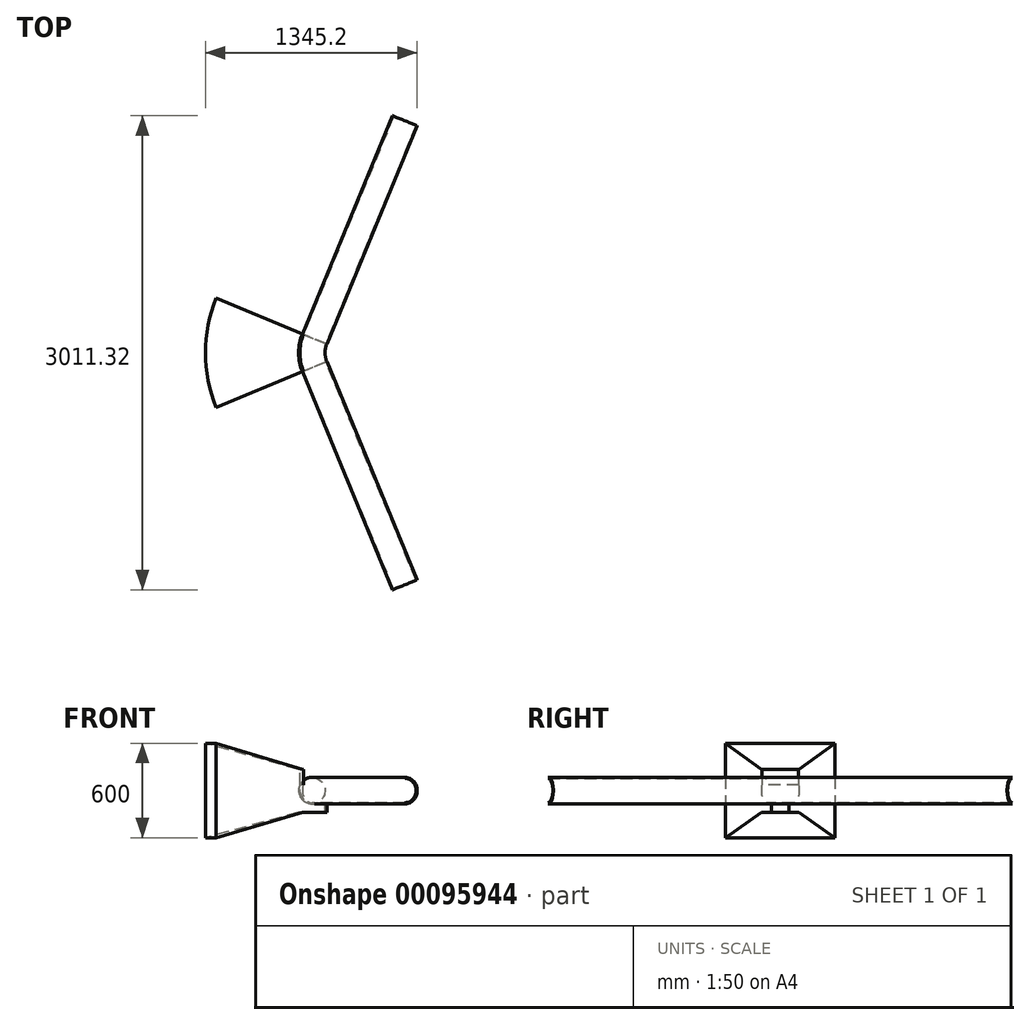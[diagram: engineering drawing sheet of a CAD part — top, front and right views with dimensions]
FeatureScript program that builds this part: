
annotation { "Feature Type Name" : "Feature", "Feature Type Description" : "" }
export const myFeature = defineFeature(function(context is Context, id is Id, definition is map)
    precondition{}
    {
        {
            var Q0;
            Q0=qCreatedBy(makeId("Front.planeOp"),FACE);
            var sketch = newSketch(context, id + "F0", { "sketchPlane" : qUnion([Q0])});
            skCircle(sketch, "E0", {"center": v(0, 0) * mm, "radius": 77.05 * mm});
            skCircle(sketch, "E1.0", {"center": v(0, 0) * mm, "radius": 84.15 * mm});
            skLineSegment(sketch, "E2", {"start": v(229, 111.57) * mm, "end": v(229, -112.44) * mm, "construction": true});
            skSolve(sketch);
        }
        {
            var Q0;
            Q0=makeQuery(id+"F0.imprint","IMPRINT",FACE,{"disambiguationData":[TD([[makeQuery(id+"F0.imprint","IMPRINT",EDGE,{"derivedFrom":sQuery(id+"F0.wireOp",EDGE,"E0")}),-1.0]])]});
            var Q1;
            Q1=sQuery(id+"F0.wireOp",EDGE,"E2");
            revolve(context, id + "F1", {"entities" : qUnion([Q0]), "axis" : qUnion([Q1]), "revolveType" : RevolveType.SYMMETRIC, "angle" : 45 * degree});
        }
        {
            var Q0;
            Q0=makeQuery(id+"F1.opRevolve","CAP_FACE",FACE,{"disambiguationData":[OSD([sQuery(id+"F0.wireOp",EDGE,"E0"),sQuery(id+"F0.wireOp",EDGE,"E1.0")])],"isStart":true});
            var sketch = newSketch(context, id + "F2", { "sketchPlane" : qUnion([Q0])});
            skCircle(sketch, "E3.0", {"center": v(-17.43, 0) * mm, "radius": 84.15 * mm});
            skCircle(sketch, "E4.0", {"center": v(-17.43, 0) * mm, "radius": 77.05 * mm});
            skSolve(sketch);
        }
        {
            var Q0;
            Q0=makeQuery(id+"F2.imprint","IMPRINT",FACE,{"disambiguationData":[TD([[makeQuery(id+"F2.imprint","IMPRINT",EDGE,{"derivedFrom":sQuery(id+"F2.wireOp",EDGE,"E3.0")}),1.0]])]});
            extrude(context, id + "F3", {"entities" : qUnion([Q0]), "operationType" : NewBodyOperationType.ADD, "depth" : 1500 * mm});
        }
        {
            var Q0;
            Q0=makeQuery(id+"F1.opRevolve","CAP_FACE",FACE,{"disambiguationData":[OSD([sQuery(id+"F0.wireOp",EDGE,"E0"),sQuery(id+"F0.wireOp",EDGE,"E1.0")])],"isStart":false});
            var sketch = newSketch(context, id + "F4", { "sketchPlane" : qUnion([Q0])});
            skCircle(sketch, "E5.0", {"center": v(17.43, 0) * mm, "radius": 84.15 * mm});
            skCircle(sketch, "E6.0", {"center": v(17.43, 0) * mm, "radius": 77.05 * mm});
            skSolve(sketch);
        }
        {
            var Q0;
            Q0=makeQuery(id+"F4.imprint","IMPRINT",FACE,{"disambiguationData":[TD([[makeQuery(id+"F4.imprint","IMPRINT",EDGE,{"derivedFrom":sQuery(id+"F4.wireOp",EDGE,"E5.0")}),-1.0]])]});
            extrude(context, id + "F5", {"entities" : qUnion([Q0]), "operationType" : NewBodyOperationType.ADD, "depth" : 1500 * mm});
        }
        {
            var Q0;
            Q0=qCreatedBy(makeId("Front.planeOp"),FACE);
            var sketch = newSketch(context, id + "F6", { "sketchPlane" : qUnion([Q0])});
            skCircle(sketch, "E7", {"center": v(0, 0) * mm, "radius": 77.05 * mm});
            skLineSegment(sketch, "E8", {"start": v(229, 146.4) * mm, "end": v(229, -165.97) * mm, "construction": true});
            skSolve(sketch);
        }
        {
            var Q0;
            Q0 = qSketchRegion(id + "F6", true);
            var Q1;
            Q1=sQuery(id+"F6.wireOp",EDGE,"E8");
            revolve(context, id + "F7", {"operationType" : NewBodyOperationType.REMOVE, "entities" : qUnion([Q0]), "axis" : qUnion([Q1]), "revolveType" : RevolveType.SYMMETRIC, "oppositeDirection" : true, "angle" : 45 * degree});
        }
        {
            var Q0;
            Q0=qCreatedBy(makeId("Front.planeOp"),FACE);
            var sketch = newSketch(context, id + "F8", { "sketchPlane" : qUnion([Q0])});
            skArc(sketch, "E9", {"start": v(-76, 35.78) * mm, "mid": v(-70.93, -45) * mm, "end": v(0, -84) * mm});
            skLineSegment(sketch, "E10", {"start": v(0, 117.65) * mm, "end": v(0, -116.35) * mm, "construction": true});
            skLineSegment(sketch, "E11", {"start": v(-76, 134.2) * mm, "end": v(-76, 35.78) * mm});
            skLineSegment(sketch, "E12", {"start": v(0, -84) * mm, "end": v(84, -84) * mm});
            skLineSegment(sketch, "E13", {"start": v(0, 0) * mm, "end": v(-876.08, 0) * mm, "construction": true});
            skLineSegment(sketch, "E14.0", {"start": v(-676, 300) * mm, "end": v(-676, -300) * mm});
            skLineSegment(sketch, "E15", {"start": v(84, -84) * mm, "end": v(84, -139.8) * mm});
            skLineSegment(sketch, "E16", {"start": v(84, -139.8) * mm, "end": v(-84, -139.8) * mm});
            skLineSegment(sketch, "E17", {"start": v(-84, -139.8) * mm, "end": v(-676, -300) * mm});
            skLineSegment(sketch, "E18", {"start": v(-84, -139.8) * mm, "end": v(-84, 181.2) * mm, "construction": true});
            skLineSegment(sketch, "E19", {"start": v(-76, 134.2) * mm, "end": v(-84, 134.2) * mm});
            skLineSegment(sketch, "E20", {"start": v(-84, 134.2) * mm, "end": v(-676, 300) * mm});
            skLineSegment(sketch, "E21", {"start": v(229, 199.65) * mm, "end": v(229, -213.04) * mm, "construction": true});
            skSolve(sketch);
        }
        {
            var Q0;
            Q0=makeQuery(id+"F8.imprint","IMPRINT",FACE,{"disambiguationData":[TD([[makeQuery(id+"F8.imprint","IMPRINT",EDGE,{"derivedFrom":sQuery(id+"F8.wireOp",EDGE,"E9")}),-1.0]])]});
            var Q1;
            Q1=sQuery(id+"F8.wireOp",EDGE,"E21");
            revolve(context, id + "F9", {"entities" : qUnion([Q0]), "axis" : qUnion([Q1]), "revolveType" : RevolveType.SYMMETRIC, "angle" : 45 * degree});
        }
    });
